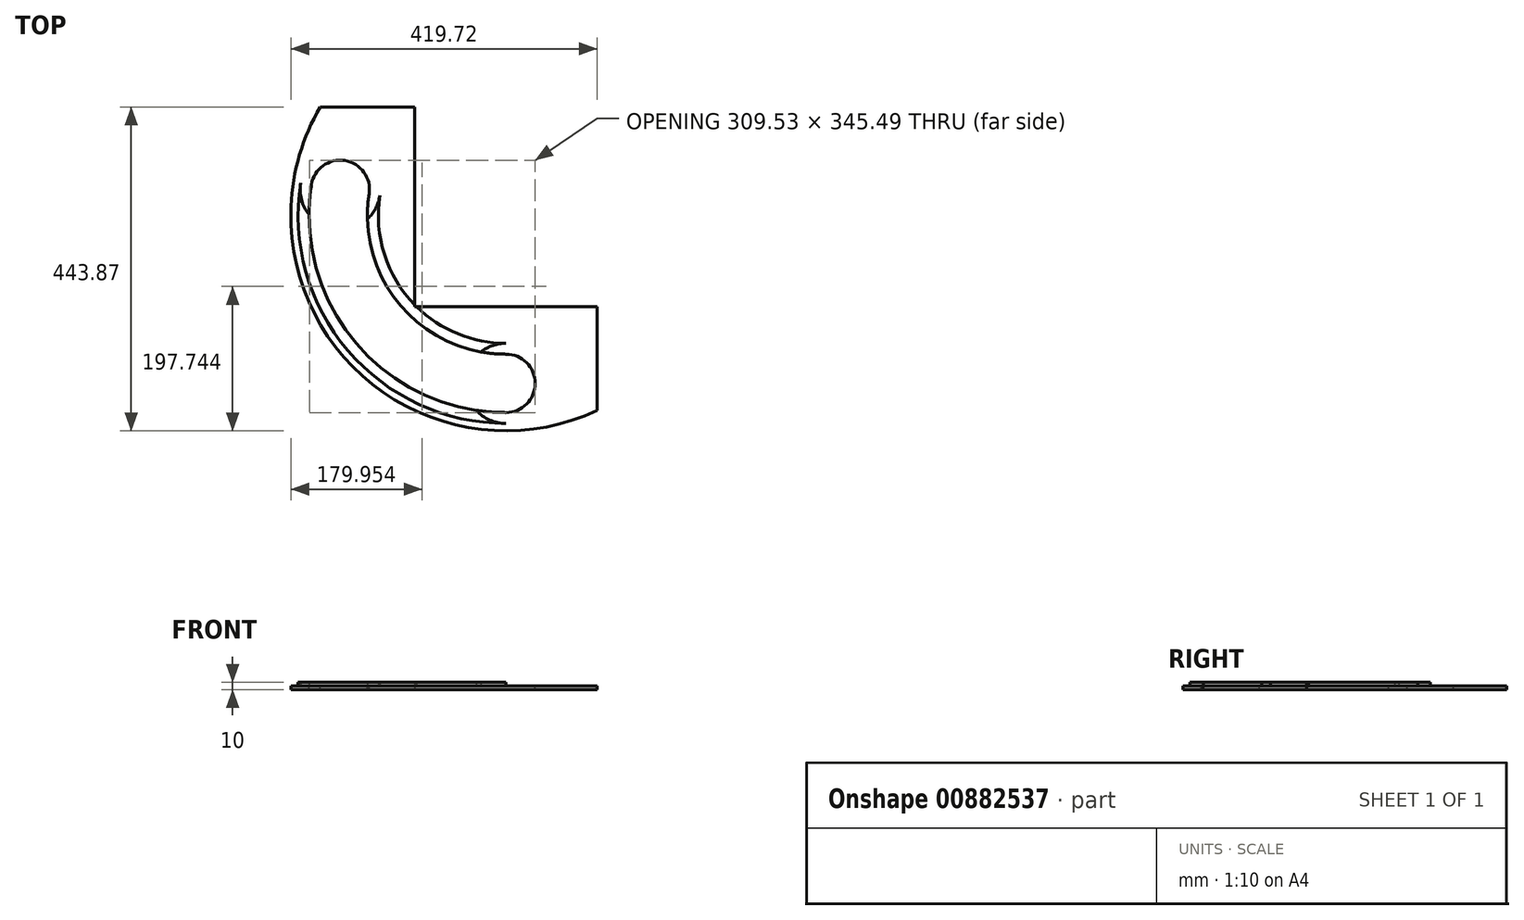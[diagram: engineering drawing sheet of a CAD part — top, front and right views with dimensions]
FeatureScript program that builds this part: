
annotation { "Feature Type Name" : "Feature", "Feature Type Description" : "" }
export const myFeature = defineFeature(function(context is Context, id is Id, definition is map)
    precondition{}
    {
        {
            var Q0;
            Q0=qCreatedBy(makeId("Top.planeOp"),FACE);
            var sketch = newSketch(context, id + "F0", { "sketchPlane" : qUnion([Q0])});
            skLineSegment(sketch, "E0.bottom", {"start": v(125, -125) * mm, "end": v(-125, -125) * mm});
            skLineSegment(sketch, "E0.top", {"start": v(125, 125) * mm, "end": v(-125, 125) * mm});
            skLineSegment(sketch, "E0.left", {"start": v(125, -125) * mm, "end": v(125, 125) * mm});
            skLineSegment(sketch, "E0.right", {"start": v(-125, -125) * mm, "end": v(-125, 125) * mm});
            skPoint(sketch, "E0.middle", {"position": v(0, 0) * mm});
            skLineSegment(sketch, "E1", {"start": v(0, 0) * mm, "end": v(-125, 0) * mm, "construction": true});
            skLineSegment(sketch, "E2.bottom", {"start": v(-349.96, 0) * mm, "end": v(0, 0) * mm});
            skLineSegment(sketch, "E2.left", {"start": v(-349.96, 0) * mm, "end": v(-349.96, 125) * mm});
            skLineSegment(sketch, "E2.right", {"start": v(125, 0) * mm, "end": v(125, 125) * mm});
            skLineSegment(sketch, "E3.MirrorCS", {"start": v(-349.96, 0) * mm, "end": v(-349.96, -249.62) * mm});
            skLineSegment(sketch, "E4.MirrorCS", {"start": v(-349.96, -249.62) * mm, "end": v(125, -249.62) * mm});
            skLineSegment(sketch, "E5.MirrorCS", {"start": v(125, 0) * mm, "end": v(125, -249.62) * mm});
            skLineSegment(sketch, "E6", {"start": v(-349.96, 125) * mm, "end": v(125, 125) * mm});
            skPoint(sketch, "E2.top.start.orphan", {"position": v(-349.96, 249.62) * mm});
            skPoint(sketch, "E7.orphan", {"position": v(125, 249.62) * mm});
            skLineSegment(sketch, "E8", {"start": v(-349.96, 29.15) * mm, "end": v(-125, 29.15) * mm});
            skLineSegment(sketch, "E9", {"start": v(-349.96, -249.62) * mm, "end": v(-349.96, -298.58) * mm});
            skLineSegment(sketch, "E10", {"start": v(-349.96, -298.58) * mm, "end": v(124.79, -298.58) * mm});
            skLineSegment(sketch, "E11", {"start": v(124.79, -298.58) * mm, "end": v(125, -249.62) * mm});
            skLineSegment(sketch, "E12", {"start": v(-294.72, 29.15) * mm, "end": v(-294.72, -298.58) * mm});
            skLineSegment(sketch, "E13", {"start": v(-294.72, 29.15) * mm, "end": v(-294.72, 125) * mm});
            skLineSegment(sketch, "E14", {"start": v(-294.72, 125) * mm, "end": v(-294.72, 148.87) * mm});
            skLineSegment(sketch, "E15", {"start": v(-294.72, 148.87) * mm, "end": v(-125.13, 148.87) * mm});
            skLineSegment(sketch, "E16", {"start": v(-125.13, 148.87) * mm, "end": v(-125, 125) * mm});
            skSolve(sketch);
        }
        {
            var Q0;
            {var subQ0=sQuery(id+"F0.wireOp",EDGE,"E8");var subQ1=sQuery(id+"F0.wireOp",EDGE,"E0.right");var subQ2=makeQuery(id+"F0.imprint","INTERSECT",VERTEX,{"derivedFrom":[subQ1,subQ0]});Q0=makeQuery(id+"F0.imprint","IMPRINT",FACE,{"disambiguationData":[TD([[makeQuery(id+"F0.imprint","IMPRINT",EDGE,{"disambiguationData":[TD([[subQ2,1.0]])],"derivedFrom":subQ1}),1.0]])]});}
            var Q1;
            {var subQ5=sQuery(id+"F0.wireOp",EDGE,"E0.bottom");Q1=makeQuery(id+"F0.imprint","IMPRINT",FACE,{"disambiguationData":[TD([[makeQuery(id+"F0.imprint","IMPRINT",EDGE,{"derivedFrom":subQ5}),1.0]])]});}
            var Q2;
            {var subQ0=sQuery(id+"F0.wireOp",EDGE,"E11");Q2=makeQuery(id+"F0.imprint","IMPRINT",FACE,{"disambiguationData":[TD([[makeQuery(id+"F0.imprint","IMPRINT",EDGE,{"derivedFrom":subQ0}),1.0]])]});}
            var Q3;
            {var subQ4=sQuery(id+"F0.wireOp",EDGE,"E6");var subQ5=sQuery(id+"F0.wireOp",EDGE,"E0.right");var subQ6=makeQuery(id+"F0.imprint","INTERSECT",VERTEX,{"derivedFrom":[subQ5,subQ4]});Q3=makeQuery(id+"F0.imprint","IMPRINT",FACE,{"disambiguationData":[TD([[makeQuery(id+"F0.imprint","IMPRINT",EDGE,{"disambiguationData":[TD([[subQ6,1.0]])],"derivedFrom":subQ5}),1.0]])]});}
            var Q4;
            {var subQ2=sQuery(id+"F0.wireOp",EDGE,"E14");Q4=makeQuery(id+"F0.imprint","IMPRINT",FACE,{"disambiguationData":[TD([[makeQuery(id+"F0.imprint","IMPRINT",EDGE,{"derivedFrom":subQ2}),-1.0]])]});}
            extrude(context, id + "F1", {"entities" : qUnion([Q0, Q1, Q2, Q3, Q4]), "depth" : 5 * mm, "offsetDistance" : 25 * mm});
        }
        {
            var Q0;
            Q0=makeQuery(id+"F1.opExtrude","CAP_FACE",FACE,{"disambiguationData":[OSD([sQuery(id+"F0.wireOp",EDGE,"E0.bottom"),sQuery(id+"F0.wireOp",EDGE,"E0.top"),sQuery(id+"F0.wireOp",EDGE,"E0.left"),sQuery(id+"F0.wireOp",EDGE,"E0.right"),sQuery(id+"F0.wireOp",EDGE,"E2.top"),sQuery(id+"F0.wireOp",EDGE,"E2.left"),sQuery(id+"F0.wireOp",EDGE,"E2.right"),sQuery(id+"F0.wireOp",EDGE,"E3.MirrorCS"),sQuery(id+"F0.wireOp",EDGE,"E4.MirrorCS"),sQuery(id+"F0.wireOp",EDGE,"E5.MirrorCS")])],"isStart":false});
            var sketch = newSketch(context, id + "F2", { "sketchPlane" : qUnion([Q0])});
            skCircle(sketch, "E17", {"center": v(0, 0) * mm, "radius": 270 * mm});
            skCircle(sketch, "E18", {"center": v(0, 0) * mm, "radius": 190 * mm});
            skLineSegment(sketch, "E19", {"start": v(0, 0) * mm, "end": v(-270, 0) * mm, "construction": true});
            skCircle(sketch, "E20", {"center": v(0, 0) * mm, "radius": 230 * mm, "construction": true});
            skCircle(sketch, "E21", {"center": v(-227.17, 35.98) * mm, "radius": 40 * mm});
            skCircle(sketch, "E22", {"center": v(0, -230) * mm, "radius": 40 * mm});
            skLineSegment(sketch, "E23", {"start": v(-227.17, 35.98) * mm, "end": v(0, 0) * mm, "construction": true});
            skLineSegment(sketch, "E24", {"start": v(0, 0) * mm, "end": v(0, -230) * mm, "construction": true});
            skSolve(sketch);
        }
        {
            var Q0;
            {var subQ0=sQuery(id+"F2.wireOp",EDGE,"E21");var subQ1=sQuery(id+"F2.wireOp",EDGE,"E17");var subQ2=makeQuery(id+"F2.imprint","INTERSECT",VERTEX,{"derivedFrom":[subQ1,subQ0]});Q0=makeQuery(id+"F2.imprint","IMPRINT",FACE,{"disambiguationData":[TD([[makeQuery(id+"F2.imprint","IMPRINT",EDGE,{"disambiguationData":[TD([[subQ2,-1.0]])],"derivedFrom":subQ1}),1.0]])]});}
            var Q1;
            {var subQ0=sQuery(id+"F2.wireOp",EDGE,"E21");var subQ1=makeQuery(id+"F2.imprint","INTERSECT",VERTEX,{"derivedFrom":[sQuery(id+"F2.wireOp",EDGE,"E17"),subQ0]});Q1=makeQuery(id+"F2.imprint","IMPRINT",FACE,{"disambiguationData":[TD([[makeQuery(id+"F2.imprint","IMPRINT",EDGE,{"disambiguationData":[TD([[subQ1,-1.0]])],"derivedFrom":subQ0}),1.0]])]});}
            var Q2;
            {var subQ0=sQuery(id+"F2.wireOp",EDGE,"E22");var subQ1=makeQuery(id+"F2.imprint","INTERSECT",VERTEX,{"derivedFrom":[sQuery(id+"F2.wireOp",EDGE,"E17"),subQ0]});Q2=makeQuery(id+"F2.imprint","IMPRINT",FACE,{"disambiguationData":[TD([[makeQuery(id+"F2.imprint","IMPRINT",EDGE,{"disambiguationData":[TD([[subQ1,1.0]])],"derivedFrom":subQ0}),1.0]])]});}
            var Q3;
            {var subQ0=sQuery(id+"F2.wireOp",EDGE,"E22");var subQ1=makeQuery(id+"F2.imprint","INTERSECT",VERTEX,{"derivedFrom":[sQuery(id+"F2.wireOp",EDGE,"E18"),subQ0]});Q3=makeQuery(id+"F2.imprint","IMPRINT",FACE,{"disambiguationData":[TD([[makeQuery(id+"F2.imprint","IMPRINT",EDGE,{"disambiguationData":[TD([[subQ1,-1.0]])],"derivedFrom":subQ0}),1.0]])]});}
            extrude(context, id + "F3", {"entities" : qUnion([Q0, Q1, Q2, Q3]), "operationType" : NewBodyOperationType.REMOVE, "oppositeDirection" : true, "depth" : 6 * mm, "offsetDistance" : 25 * mm});
        }
        {
            var Q0;
            Q0=makeQuery(id+"F1.opExtrude","CAP_FACE",FACE,{"disambiguationData":[OSD([sQuery(id+"F0.wireOp",EDGE,"E0.bottom"),sQuery(id+"F0.wireOp",EDGE,"E0.right"),sQuery(id+"F0.wireOp",EDGE,"E5.MirrorCS"),sQuery(id+"F0.wireOp",EDGE,"E8"),sQuery(id+"F0.wireOp",EDGE,"E10"),sQuery(id+"F0.wireOp",EDGE,"E11"),sQuery(id+"F0.wireOp",EDGE,"E12")])],"isStart":false});
            var sketch = newSketch(context, id + "F4", { "sketchPlane" : qUnion([Q0])});
            skCircle(sketch, "E25", {"center": v(0, 0) * mm, "radius": 295 * mm});
            skLineSegment(sketch, "E26", {"start": v(178.33, -235) * mm, "end": v(178.33, -361.67) * mm});
            skLineSegment(sketch, "E27", {"start": v(178.33, -361.67) * mm, "end": v(-429.48, -361.67) * mm});
            skLineSegment(sketch, "E28", {"start": v(-429.48, -361.67) * mm, "end": v(-429.48, 76.22) * mm});
            skLineSegment(sketch, "E29", {"start": v(-429.48, 76.22) * mm, "end": v(-284.98, 76.22) * mm});
            skSolve(sketch);
        }
        {
            var Q0;
            {var subQ0=sQuery(id+"F4.wireOp",EDGE,"E25");var subQ1=makeQuery(id+"F1.opExtrude","CAP_EDGE",EDGE,{"disambiguationData":[OSD([sQuery(id+"F0.wireOp",EDGE,"E12")])],"isStart":false});var subQ2=makeQuery(id+"F4.imprint","INTERSECT",VERTEX,{"disambiguationData":[OD(0.0)],"derivedFrom":[subQ1,subQ0]});Q0=makeQuery(id+"F4.imprint","IMPRINT",FACE,{"disambiguationData":[TD([[makeQuery(id+"F4.imprint","IMPRINT",EDGE,{"disambiguationData":[TD([[subQ2,-1.0]])],"derivedFrom":subQ0}),1.0]])]});}
            var Q1;
            {var subQ0=sQuery(id+"F4.wireOp",EDGE,"E25");var subQ1=makeQuery(id+"F1.opExtrude","CAP_EDGE",EDGE,{"disambiguationData":[OSD([sQuery(id+"F0.wireOp",EDGE,"E8")])],"isStart":false});var subQ2=makeQuery(id+"F4.imprint","INTERSECT",VERTEX,{"derivedFrom":[subQ1,subQ0]});Q1=makeQuery(id+"F4.imprint","IMPRINT",FACE,{"disambiguationData":[TD([[makeQuery(id+"F4.imprint","IMPRINT",EDGE,{"disambiguationData":[TD([[subQ2,-1.0]])],"derivedFrom":subQ0}),-1.0]])]});}
            var Q2;
            {var subQ11=sQuery(id+"F4.wireOp",EDGE,"E26");Q2=makeQuery(id+"F4.imprint","IMPRINT",FACE,{"disambiguationData":[TD([[makeQuery(id+"F4.imprint","IMPRINT",EDGE,{"derivedFrom":subQ11}),-1.0]])]});}
            var Q3;
            {var subQ5=makeQuery(id+"F1.opExtrude","CAP_EDGE",EDGE,{"disambiguationData":[OSD([sQuery(id+"F0.wireOp",EDGE,"E10")])],"isStart":false});Q3=makeQuery(id+"F4.imprint","IMPRINT",FACE,{"disambiguationData":[TD([[makeQuery(id+"F4.imprint","IMPRINT",EDGE,{"derivedFrom":subQ5}),1.0]])]});}
            var Q4;
            {var subQ0=sQuery(id+"F4.wireOp",EDGE,"E29");var subQ1=sQuery(id+"F4.wireOp",EDGE,"E25");var subQ2=makeQuery(id+"F4.imprint","INTERSECT",VERTEX,{"derivedFrom":[subQ1,subQ0]});Q4=makeQuery(id+"F4.imprint","IMPRINT",FACE,{"disambiguationData":[TD([[makeQuery(id+"F4.imprint","IMPRINT",EDGE,{"disambiguationData":[TD([[subQ2,-1.0]])],"derivedFrom":subQ1}),-1.0]])]});}
            var Q5;
            {var subQ0=sQuery(id+"F4.wireOp",EDGE,"E29");var subQ1=sQuery(id+"F4.wireOp",EDGE,"E25");var subQ2=makeQuery(id+"F4.imprint","INTERSECT",VERTEX,{"derivedFrom":[subQ1,subQ0]});Q5=makeQuery(id+"F4.imprint","IMPRINT",FACE,{"disambiguationData":[TD([[makeQuery(id+"F4.imprint","IMPRINT",EDGE,{"disambiguationData":[TD([[subQ2,1.0]])],"derivedFrom":subQ1}),-1.0]])]});}
            extrude(context, id + "F5", {"entities" : qUnion([Q0, Q1, Q2, Q3, Q4, Q5]), "operationType" : NewBodyOperationType.REMOVE, "oppositeDirection" : true, "depth" : 25 * mm, "offsetDistance" : 25 * mm});
        }
        {
            var Q0;
            Q0=makeQuery(id+"F1.opExtrude","CAP_FACE",FACE,{"disambiguationData":[OSD([sQuery(id+"F0.wireOp",EDGE,"E0.bottom"),sQuery(id+"F0.wireOp",EDGE,"E0.right"),sQuery(id+"F0.wireOp",EDGE,"E5.MirrorCS"),sQuery(id+"F0.wireOp",EDGE,"E10"),sQuery(id+"F0.wireOp",EDGE,"E11"),sQuery(id+"F0.wireOp",EDGE,"E12"),sQuery(id+"F0.wireOp",EDGE,"E13"),sQuery(id+"F0.wireOp",EDGE,"E14"),sQuery(id+"F0.wireOp",EDGE,"E15"),sQuery(id+"F0.wireOp",EDGE,"E16")])],"isStart":false});
            var sketch = newSketch(context, id + "F6", { "sketchPlane" : qUnion([Q0])});
            skCircle(sketch, "E30", {"center": v(0, -230) * mm, "radius": 55 * mm});
            skCircle(sketch, "E31", {"center": v(-227.17, 35.98) * mm, "radius": 55 * mm});
            skCircle(sketch, "E32", {"center": v(0, 0) * mm, "radius": 175 * mm});
            skCircle(sketch, "E33", {"center": v(0, 0) * mm, "radius": 285 * mm});
            skSolve(sketch);
        }
        {
            var Q0;
            {var subQ0=makeQuery(id+"F3.boolean.opBoolean","COPY",EDGE,{"derivedFrom":makeQuery(id+"F3.opExtrude","CAP_EDGE",EDGE,{"disambiguationData":[OSD([sQuery(id+"F2.wireOp",EDGE,"E21")])],"isStart":true})});Q0=makeQuery(id+"F6.imprint","IMPRINT",FACE,{"disambiguationData":[TD([[makeQuery(id+"F6.imprint","IMPRINT",EDGE,{"derivedFrom":subQ0}),-1.0]])]});}
            var Q1;
            {var subQ0=sQuery(id+"F6.wireOp",EDGE,"E32");var subQ5=sQuery(id+"F6.wireOp",EDGE,"E30");var subQ6=makeQuery(id+"F6.imprint","INTERSECT",VERTEX,{"derivedFrom":[subQ5,subQ0]});Q1=makeQuery(id+"F6.imprint","IMPRINT",FACE,{"disambiguationData":[TD([[makeQuery(id+"F6.imprint","IMPRINT",EDGE,{"disambiguationData":[TD([[subQ6,-1.0]])],"derivedFrom":subQ5}),-1.0]])]});}
            var Q2;
            {var subQ0=sQuery(id+"F6.wireOp",EDGE,"E33");var subQ1=sQuery(id+"F6.wireOp",EDGE,"E30");var subQ2=makeQuery(id+"F6.imprint","INTERSECT",VERTEX,{"derivedFrom":[subQ1,subQ0]});Q2=makeQuery(id+"F6.imprint","IMPRINT",FACE,{"disambiguationData":[TD([[makeQuery(id+"F6.imprint","IMPRINT",EDGE,{"disambiguationData":[TD([[subQ2,1.0]])],"derivedFrom":subQ1}),-1.0]])]});}
            var Q3;
            {var subQ0=makeQuery(id+"F3.boolean.opBoolean","COPY",EDGE,{"derivedFrom":makeQuery(id+"F3.opExtrude","CAP_EDGE",EDGE,{"disambiguationData":[OSD([sQuery(id+"F2.wireOp",EDGE,"E22")])],"isStart":true})});Q3=makeQuery(id+"F6.imprint","IMPRINT",FACE,{"disambiguationData":[TD([[makeQuery(id+"F6.imprint","IMPRINT",EDGE,{"derivedFrom":subQ0}),-1.0]])]});}
            extrude(context, id + "F7", {"entities" : qUnion([Q0, Q1, Q2, Q3]), "depth" : 5 * mm, "offsetDistance" : 25 * mm});
        }
    });
